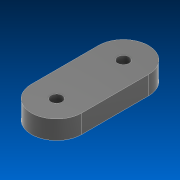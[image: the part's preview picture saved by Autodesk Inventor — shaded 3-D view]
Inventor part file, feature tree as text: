
AUTODESK INVENTOR PART (.ipt)
format: ipt  version: 2022.2 (Build 262287000, 287)  size: 94,208 bytes
history: native  units: in
note: dims shown in document units (in); Inventor stores cm internally (conversion verified against a paired STEP export)
features: extrude x1, sketch x1
ambient origin geometry x8: Origin, YZ Plane, XZ Plane, XY Plane, X Axis, Y Axis, Z Axis, Center Point
bodies: Solid1 (feature_tree)
feature tree (2):
  extrude  "Extrusion1"  Depth=1.0in
  sketch  "Sketch1"  dims[d0=0.17in d2=1.0in d3=0.75in d4=0.278in d5=0.0in]
